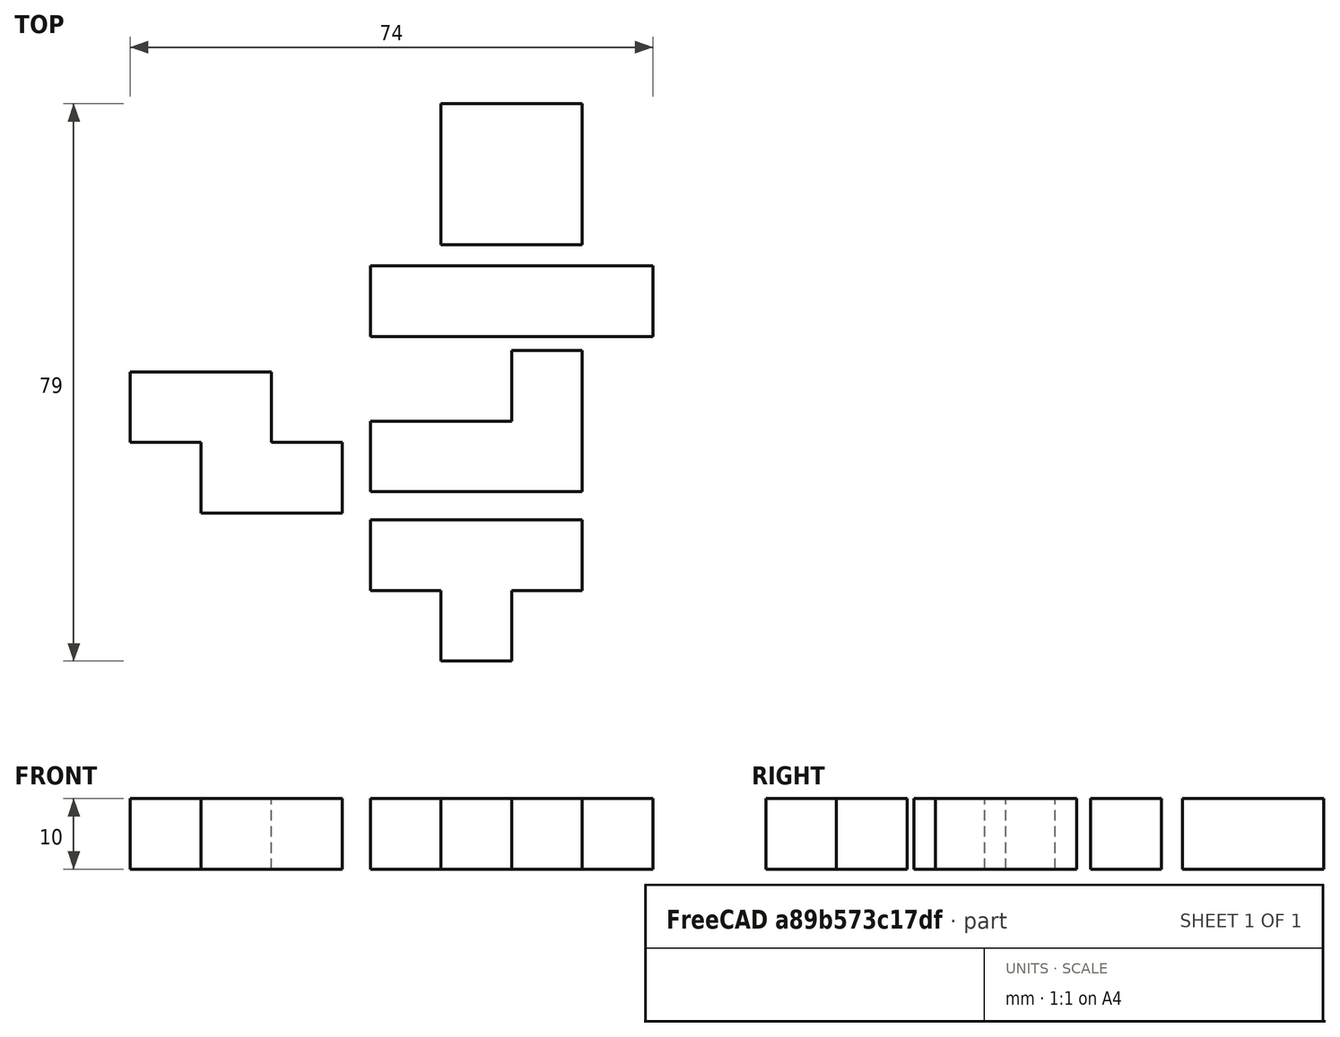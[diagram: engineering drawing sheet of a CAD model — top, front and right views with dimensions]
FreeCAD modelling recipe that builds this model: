
FCSTD DOCUMENT  (FreeCAD 0.20R29177 +426 (Git))
Label: tetris
License: All rights reserved
LicenseURL: http://en.wikipedia.org/wiki/All_rights_reserved
objects: Part::Box×17, Part::MultiFuse×8
note: 25 computed .brp shape members not serialized (recipe doc carries the construction recipe); baked Part::Feature solids carry a one-line shape summary decoded from their .brp

FEATURE [Part::Box] Box  label="Cubo"
  AttacherType = Attacher::AttachEngine3D
  Height = 10
  Length = 10
  Placement = pos=(10,0,0) rot=(0,0,1;0rad)
  Width = 10
FEATURE [Part::Box] Box001  label="Cubo001"
  AttacherType = Attacher::AttachEngine3D
  Height = 10
  Length = 10
  Width = 10
FEATURE [Part::Box] Box002  label="Cubo002"
  AttacherType = Attacher::AttachEngine3D
  Height = 10
  Length = 10
  Placement = pos=(20,0,0) rot=(0,0,1;0rad)
  Width = 10
FEATURE [Part::Box] Box003  label="Cubo003"
  AttacherType = Attacher::AttachEngine3D
  Height = 10
  Length = 10
  Placement = pos=(-10,0,0) rot=(0,0,1;0rad)
  Width = 10
FEATURE [Part::MultiFuse] Fusion
  Refine = true
  Shapes = -> [Box,Box001]
FEATURE [Part::MultiFuse] Fusion001
  Refine = true
  Shapes = -> [Box,Box001,Fusion,Box003]
FEATURE [Part::MultiFuse] Fusion002
  Placement = pos=(0,19,0) rot=(0,0,1;0rad)
  Refine = true
  Shapes = -> [Box,Box001,Fusion,Box003,Fusion001,Box002]
FEATURE [Part::Box] Box004  label="Cubo004"
  AttacherType = Attacher::AttachEngine3D
  Height = 10
  Length = 10
  Placement = pos=(-10,0,0) rot=(0,0,1;0rad)
  Width = 10
FEATURE [Part::Box] Box005  label="Cubo005"
  AttacherType = Attacher::AttachEngine3D
  Height = 10
  Length = 10
  Placement = pos=(0,-10,0) rot=(0,0,1;0rad)
  Width = 10
FEATURE [Part::Box] Box006  label="Cubo006"
  AttacherType = Attacher::AttachEngine3D
  Height = 10
  Length = 10
  Placement = pos=(10,0,0) rot=(0,0,1;0rad)
  Width = 10
FEATURE [Part::Box] Box007  label="Cubo007"
  AttacherType = Attacher::AttachEngine3D
  Height = 10
  Length = 10
  Width = 10
FEATURE [Part::MultiFuse] Fusion003
  Placement = pos=(0,-17,0) rot=(0,0,1;0rad)
  Refine = true
  Shapes = -> [Box007,Box006,Box005,Box004]
FEATURE [Part::Box] Box008  label="Cubo008"
  AttacherType = Attacher::AttachEngine3D
  Height = 10
  Length = 20
  Placement = pos=(0,32,0) rot=(0,0,1;0rad)
  Width = 20
FEATURE [Part::Box] Box009  label="Cubo009"
  AttacherType = Attacher::AttachEngine3D
  Height = 10
  Length = 10
  Placement = pos=(10,0,0) rot=(0,0,1;0rad)
  Width = 10
FEATURE [Part::Box] Box010  label="Cubo010"
  AttacherType = Attacher::AttachEngine3D
  Height = 10
  Length = 10
  Width = 10
FEATURE [Part::MultiFuse] Fusion004
  Refine = true
  Shapes = -> [Box010,Box009]
FEATURE [Part::Box] Box011  label="Cubo011"
  AttacherType = Attacher::AttachEngine3D
  Height = 10
  Length = 10
  Placement = pos=(10,0,0) rot=(0,0,1;0rad)
  Width = 10
FEATURE [Part::Box] Box012  label="Cubo012"
  AttacherType = Attacher::AttachEngine3D
  Height = 10
  Length = 10
  Width = 10
FEATURE [Part::MultiFuse] Fusion005
  Placement = pos=(10,-10,0) rot=(0,0,1;0rad)
  Refine = true
  Shapes = -> [Box012,Box011]
FEATURE [Part::MultiFuse] Fusion006
  Placement = pos=(-44,4,0) rot=(0,0,1;0rad)
  Refine = true
  Shapes = -> [Fusion005,Fusion004]
FEATURE [Part::Box] Box013  label="Cubo013"
  AttacherType = Attacher::AttachEngine3D
  Height = 10
  Length = 10
  Width = 10
FEATURE [Part::Box] Box014  label="Cubo014"
  AttacherType = Attacher::AttachEngine3D
  Height = 10
  Length = 10
  Placement = pos=(-10,0,0) rot=(0,0,1;0rad)
  Width = 10
FEATURE [Part::Box] Box015  label="Cubo015"
  AttacherType = Attacher::AttachEngine3D
  Height = 10
  Length = 10
  Placement = pos=(10,0,0) rot=(0,0,1;0rad)
  Width = 10
FEATURE [Part::Box] Box016  label="Cubo016"
  AttacherType = Attacher::AttachEngine3D
  Height = 10
  Length = 10
  Placement = pos=(10,10,0) rot=(0,0,1;0rad)
  Width = 10
FEATURE [Part::MultiFuse] Fusion007
  Placement = pos=(0,-3,0) rot=(0,0,1;0rad)
  Refine = true
  Shapes = -> [Box013,Box014,Box015,Box016]
